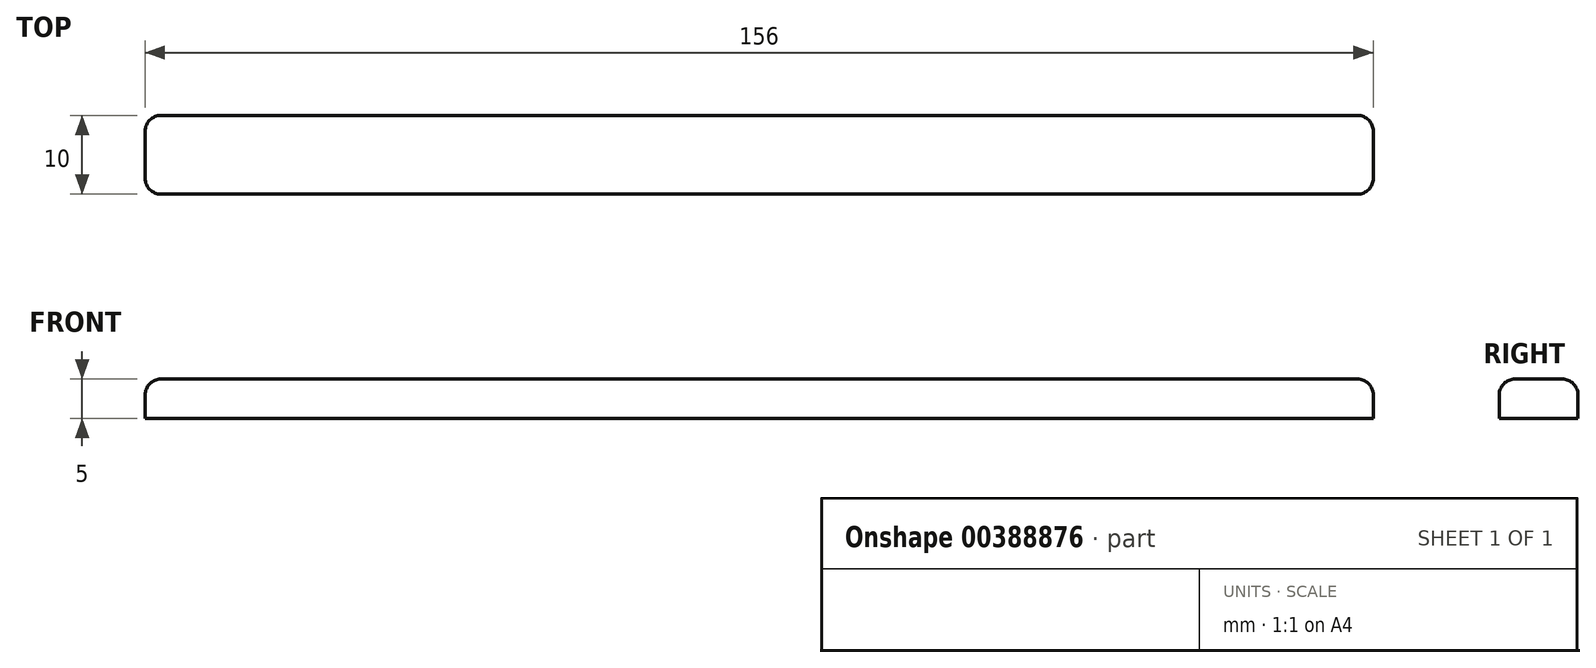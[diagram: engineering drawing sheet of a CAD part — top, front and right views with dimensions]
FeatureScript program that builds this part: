
annotation { "Feature Type Name" : "Feature", "Feature Type Description" : "" }
export const myFeature = defineFeature(function(context is Context, id is Id, definition is map)
    precondition{}
    {
        {
            var Q0;
            Q0=qCreatedBy(makeId("Top.planeOp"),FACE);
            var sketch = newSketch(context, id + "F0", { "sketchPlane" : qUnion([Q0])});
            skLineSegment(sketch, "E0.bottom", {"start": v(0, 0) * mm, "end": v(-156, 0) * mm});
            skLineSegment(sketch, "E0.top", {"start": v(0, 10) * mm, "end": v(-156, 10) * mm});
            skLineSegment(sketch, "E0.left", {"start": v(0, 0) * mm, "end": v(0, 10) * mm});
            skLineSegment(sketch, "E0.right", {"start": v(-156, 0) * mm, "end": v(-156, 10) * mm});
            skSolve(sketch);
        }
        {
            var Q0;
            Q0=makeQuery(id+"F0.imprint","IMPRINT",FACE,{"disambiguationData":[TD([[makeQuery(id+"F0.imprint","IMPRINT",EDGE,{"derivedFrom":sQuery(id+"F0.wireOp",EDGE,"E0.bottom")}),-1.0]])]});
            extrude(context, id + "F1", {"entities" : qUnion([Q0]), "depth" : 5 * mm});
        }
        {
            var Q0;
            Q0=makeQuery(id+"F1.opExtrude","CAP_EDGE",EDGE,{"disambiguationData":[OSD([sQuery(id+"F0.wireOp",EDGE,"E0.top")])],"isStart":false});
            var Q1;
            Q1=makeQuery(id+"F1.opExtrude","CAP_EDGE",EDGE,{"disambiguationData":[OSD([sQuery(id+"F0.wireOp",EDGE,"E0.right")])],"isStart":false});
            var Q2;
            Q2=makeQuery(id+"F1.opExtrude","CAP_EDGE",EDGE,{"disambiguationData":[OSD([sQuery(id+"F0.wireOp",EDGE,"E0.bottom")])],"isStart":false});
            var Q3;
            Q3=makeQuery(id+"F1.opExtrude","CAP_EDGE",EDGE,{"disambiguationData":[OSD([sQuery(id+"F0.wireOp",EDGE,"E0.left")])],"isStart":false});
            fillet(context, id + "F2", {"entities" : qUnion([Q0, Q1, Q2, Q3]), "radius" : 2 * mm, "tangentPropagation" : true, "allowEdgeOverflow" : false});
        }
        {
            var Q0;
            Q0=makeQuery(id+"F2.opFillet","BLEND_EDGE",EDGE,{"blendedFrom":[makeQuery(id+"F1.opExtrude","CAP_EDGE",EDGE,{"disambiguationData":[OSD([sQuery(id+"F0.wireOp",EDGE,"E0.top")])],"isStart":false}),makeQuery(id+"F1.opExtrude","CAP_EDGE",EDGE,{"disambiguationData":[OSD([sQuery(id+"F0.wireOp",EDGE,"E0.right")])],"isStart":false})],"blendedInto":[]});
            var Q1;
            Q1=makeQuery(id+"F2.opFillet","BLEND_EDGE",EDGE,{"blendedFrom":[makeQuery(id+"F1.opExtrude","CAP_EDGE",EDGE,{"disambiguationData":[OSD([sQuery(id+"F0.wireOp",EDGE,"E0.bottom")])],"isStart":false}),makeQuery(id+"F1.opExtrude","CAP_EDGE",EDGE,{"disambiguationData":[OSD([sQuery(id+"F0.wireOp",EDGE,"E0.right")])],"isStart":false})],"blendedInto":[]});
            var Q2;
            Q2=makeQuery(id+"F2.opFillet","BLEND_EDGE",EDGE,{"blendedFrom":[makeQuery(id+"F1.opExtrude","CAP_EDGE",EDGE,{"disambiguationData":[OSD([sQuery(id+"F0.wireOp",EDGE,"E0.bottom")])],"isStart":false}),makeQuery(id+"F1.opExtrude","CAP_EDGE",EDGE,{"disambiguationData":[OSD([sQuery(id+"F0.wireOp",EDGE,"E0.left")])],"isStart":false})],"blendedInto":[]});
            var Q3;
            Q3=makeQuery(id+"F2.opFillet","BLEND_EDGE",EDGE,{"blendedFrom":[makeQuery(id+"F1.opExtrude","CAP_EDGE",EDGE,{"disambiguationData":[OSD([sQuery(id+"F0.wireOp",EDGE,"E0.top")])],"isStart":false}),makeQuery(id+"F1.opExtrude","CAP_EDGE",EDGE,{"disambiguationData":[OSD([sQuery(id+"F0.wireOp",EDGE,"E0.left")])],"isStart":false})],"blendedInto":[]});
            fillet(context, id + "F3", {"entities" : qUnion([Q0, Q1, Q2, Q3]), "radius" : 2 * mm, "tangentPropagation" : true, "allowEdgeOverflow" : false});
        }
    });
